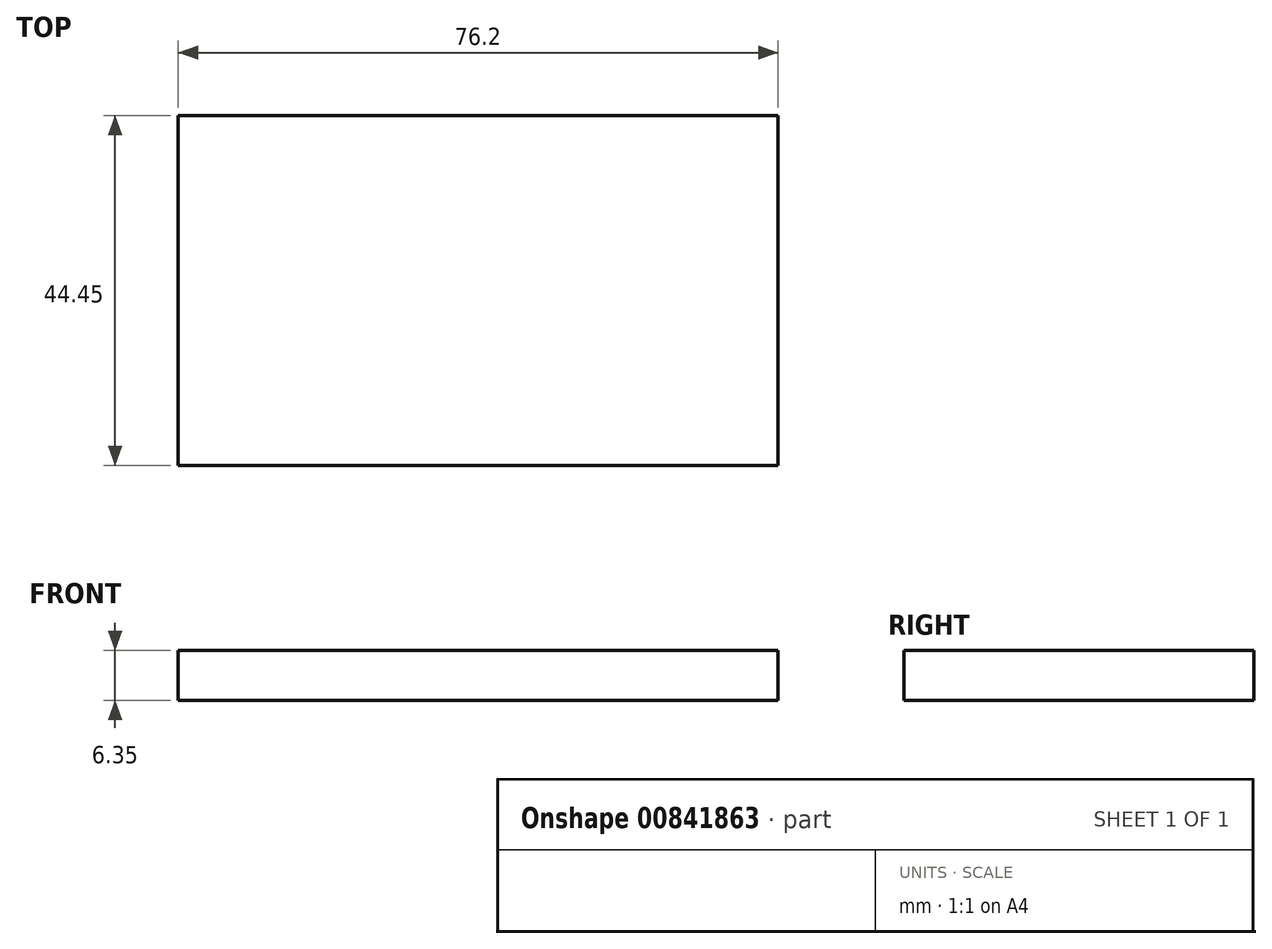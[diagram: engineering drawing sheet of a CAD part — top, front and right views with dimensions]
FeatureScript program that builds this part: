
annotation { "Feature Type Name" : "Feature", "Feature Type Description" : "" }
export const myFeature = defineFeature(function(context is Context, id is Id, definition is map)
    precondition{}
    {
        {
            var Q0;
            Q0=qCreatedBy(makeId("Top.planeOp"),FACE);
            var sketch = newSketch(context, id + "F0", { "sketchPlane" : qUnion([Q0])});
            skLineSegment(sketch, "E0.bottom", {"start": v(-24.04, 32.8) * mm, "end": v(52.16, 32.8) * mm});
            skLineSegment(sketch, "E0.top", {"start": v(-24.04, -11.65) * mm, "end": v(52.16, -11.65) * mm});
            skLineSegment(sketch, "E0.left", {"start": v(-24.04, 32.8) * mm, "end": v(-24.04, -11.65) * mm});
            skLineSegment(sketch, "E0.right", {"start": v(52.16, 32.8) * mm, "end": v(52.16, -11.65) * mm});
            skSolve(sketch);
        }
        {
            var Q0;
            Q0 = qSketchRegion(id + "F0", true);
            extrude(context, id + "F1", {"entities" : qUnion([Q0]), "depth" : 6.35 * mm, "offsetDistance" : 25.4 * mm});
        }
    });
